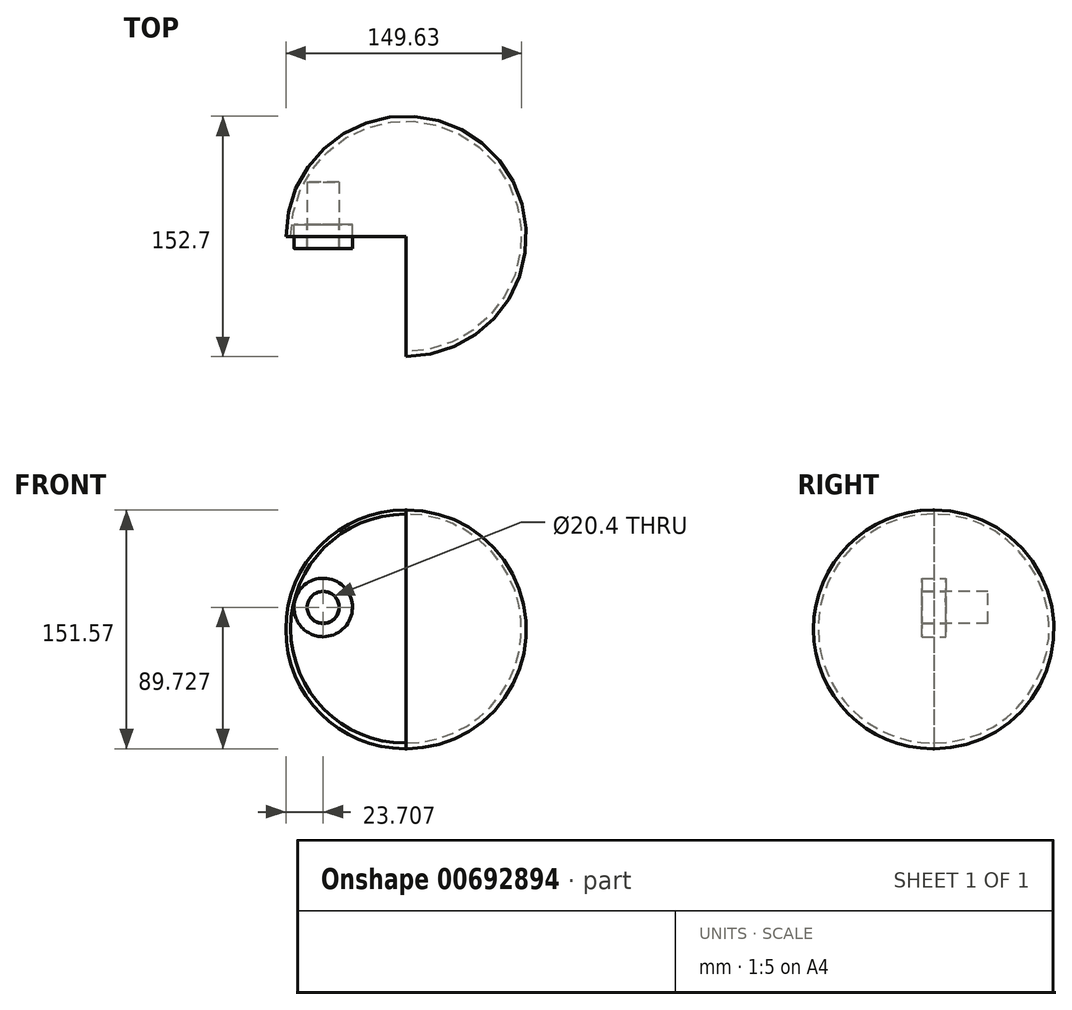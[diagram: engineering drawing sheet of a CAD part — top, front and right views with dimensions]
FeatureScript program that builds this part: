
annotation { "Feature Type Name" : "Feature", "Feature Type Description" : "" }
export const myFeature = defineFeature(function(context is Context, id is Id, definition is map)
    precondition{}
    {
        {
            var Q0;
            Q0=qCreatedBy(makeId("Front.planeOp"),FACE);
            var sketch = newSketch(context, id + "F0", { "sketchPlane" : qUnion([Q0])});
            skArc(sketch, "E0", {"start": v(0, 76.05) * mm, "mid": v(-76.35, 0.27) * mm, "end": v(0, -75.52) * mm});
            skLineSegment(sketch, "E1", {"start": v(0, 95.29) * mm, "end": v(0, -93.03) * mm, "construction": true});
            skLineSegment(sketch, "E2", {"start": v(0, 76.05) * mm, "end": v(0, -75.52) * mm});
            skSolve(sketch);
        }
        {
            var Q0;
            Q0 = qSketchRegion(id + "F0", true);
            var Q1;
            Q1=sQuery(id+"F0.wireOp",EDGE,"E1");
            revolve(context, id + "F1", {"entities" : qUnion([Q0]), "axis" : qUnion([Q1]), "revolveType" : RevolveType.ONE_DIRECTION, "angle" : 270 * degree});
        }
        {
            var Q0;
            Q0=qCreatedBy(makeId("Front.planeOp"),FACE);
            var sketch = newSketch(context, id + "F2", { "sketchPlane" : qUnion([Q0])});
            skLineSegment(sketch, "E3", {"start": v(0, 79.4) * mm, "end": v(0, -78.53) * mm, "construction": true});
            skArc(sketch, "E4", {"start": v(0, 73.47) * mm, "mid": v(-73.28, 0.78) * mm, "end": v(0, -71.9) * mm});
            skLineSegment(sketch, "E5", {"start": v(0, 73.47) * mm, "end": v(0, -71.9) * mm});
            skSolve(sketch);
        }
        {
            var Q0;
            Q0 = qSketchRegion(id + "F2", true);
            var Q1;
            Q1=sQuery(id+"F2.wireOp",EDGE,"E5");
            revolve(context, id + "F3", {"operationType" : NewBodyOperationType.REMOVE, "entities" : qUnion([Q0]), "axis" : qUnion([Q1]), "revolveType" : RevolveType.FULL, "oppositeDirection" : true});
        }
        {
            var Q0;
            Q0=qCreatedBy(makeId("Front.planeOp"),FACE);
            var sketch = newSketch(context, id + "F4", { "sketchPlane" : qUnion([Q0])});
            skCircle(sketch, "E6", {"center": v(-52.64, 14.2) * mm, "radius": 18.57 * mm});
            skCircle(sketch, "E7", {"center": v(-52.64, 14.2) * mm, "radius": 10.2 * mm});
            skSolve(sketch);
        }
        {
            var Q0;
            Q0 = qSketchRegion(id + "F4", true);
            extrude(context, id + "F5", {"entities" : qUnion([Q0]), "operationType" : NewBodyOperationType.ADD, "endBound" : BoundingType.SYMMETRIC, "depth" : 15.24 * mm, "offsetDistance" : 25.4 * mm});
        }
        {
            var Q0;
            Q0=qCreatedBy(makeId("Front.planeOp"),FACE);
            var sketch = newSketch(context, id + "F6", { "sketchPlane" : qUnion([Q0])});
            skCircle(sketch, "E8", {"center": v(-52.7, 14.27) * mm, "radius": 10.08 * mm});
            skSolve(sketch);
        }
        {
            var Q0;
            Q0 = qSketchRegion(id + "F6", true);
            extrude(context, id + "F7", {"entities" : qUnion([Q0]), "endBound" : BoundingType.SYMMETRIC, "oppositeDirection" : true, "depth" : 14.73 * mm, "offsetDistance" : 25.4 * mm});
        }
        {
            var Q0;
            Q0=makeQuery(id+"F7.opExtrude","CAP_FACE",FACE,{"disambiguationData":[OSD([sQuery(id+"F6.wireOp",EDGE,"E8")])],"isStart":true});
            extrude(context, id + "F8", {"entities" : qUnion([Q0]), "operationType" : NewBodyOperationType.ADD, "oppositeDirection" : true, "depth" : 41.9 * mm, "offsetDistance" : 25.4 * mm});
        }
    });
